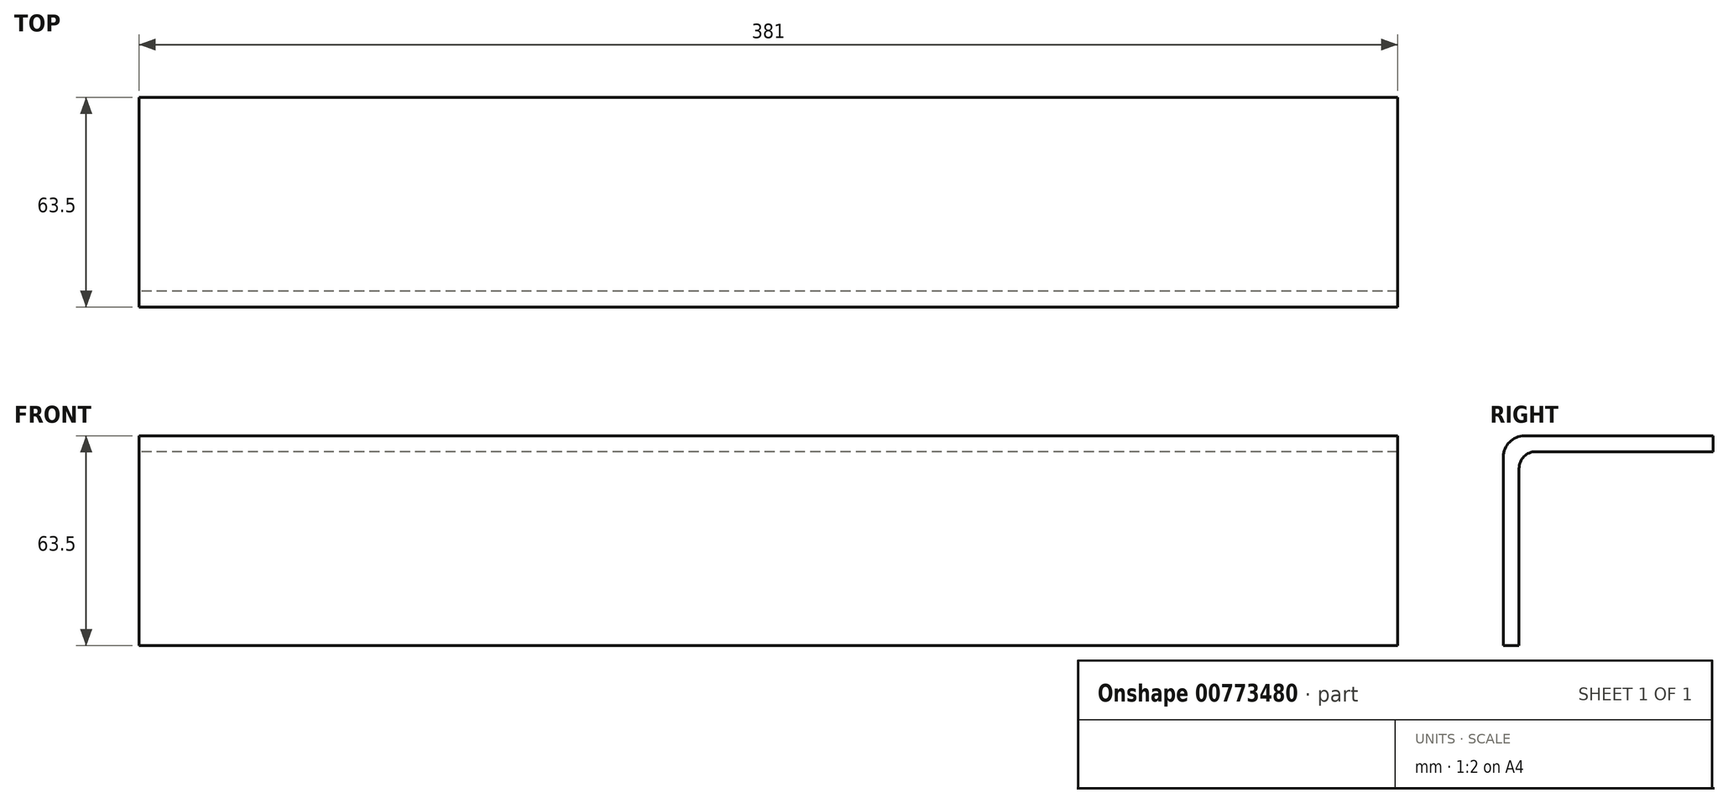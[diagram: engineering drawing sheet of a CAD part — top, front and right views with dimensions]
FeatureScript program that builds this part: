
annotation { "Feature Type Name" : "Feature", "Feature Type Description" : "" }
export const myFeature = defineFeature(function(context is Context, id is Id, definition is map)
    precondition{}
    {
        {
            var Q0;
            Q0=qCreatedBy(makeId("Right.planeOp"),FACE);
            var sketch = newSketch(context, id + "F0", { "sketchPlane" : qUnion([Q0])});
            skLineSegment(sketch, "E0", {"start": v(-28.12, -12.25) * mm, "end": v(-28.12, 44.9) * mm});
            skLineSegment(sketch, "E1", {"start": v(-21.77, 51.25) * mm, "end": v(35.38, 51.25) * mm});
            skPoint(sketch, "E2.visualSharp", {"position": v(-28.12, 51.25) * mm});
            skArc(sketch, "E2.filletArc", {"start": v(-21.77, 51.25) * mm, "mid": v(-26.26, 49.39) * mm, "end": v(-28.12, 44.9) * mm});
            skLineSegment(sketch, "E3", {"start": v(-28.12, -12.25) * mm, "end": v(-23.35, -12.25) * mm});
            skLineSegment(sketch, "E4", {"start": v(35.38, 51.25) * mm, "end": v(35.38, 46.48) * mm});
            skLineSegment(sketch, "E5", {"start": v(-23.35, -12.25) * mm, "end": v(-23.35, 41.4) * mm});
            skLineSegment(sketch, "E6", {"start": v(35.38, 46.48) * mm, "end": v(-18.27, 46.48) * mm});
            skPoint(sketch, "E7.newPointA", {"position": v(-23.35, 46.42) * mm});
            skPoint(sketch, "E7.newPointB", {"position": v(-23.29, 46.48) * mm});
            skArc(sketch, "E7.filletArc", {"start": v(-18.27, 46.48) * mm, "mid": v(-21.87, 45) * mm, "end": v(-23.35, 41.4) * mm});
            skSolve(sketch);
        }
        {
            var Q0;
            Q0=qSketchRegion(id+"F0",true);
            extrude(context, id + "F1", {"entities" : qUnion([Q0]), "depth" : 381 * mm, "offsetDistance" : 25.4 * mm});
        }
    });
